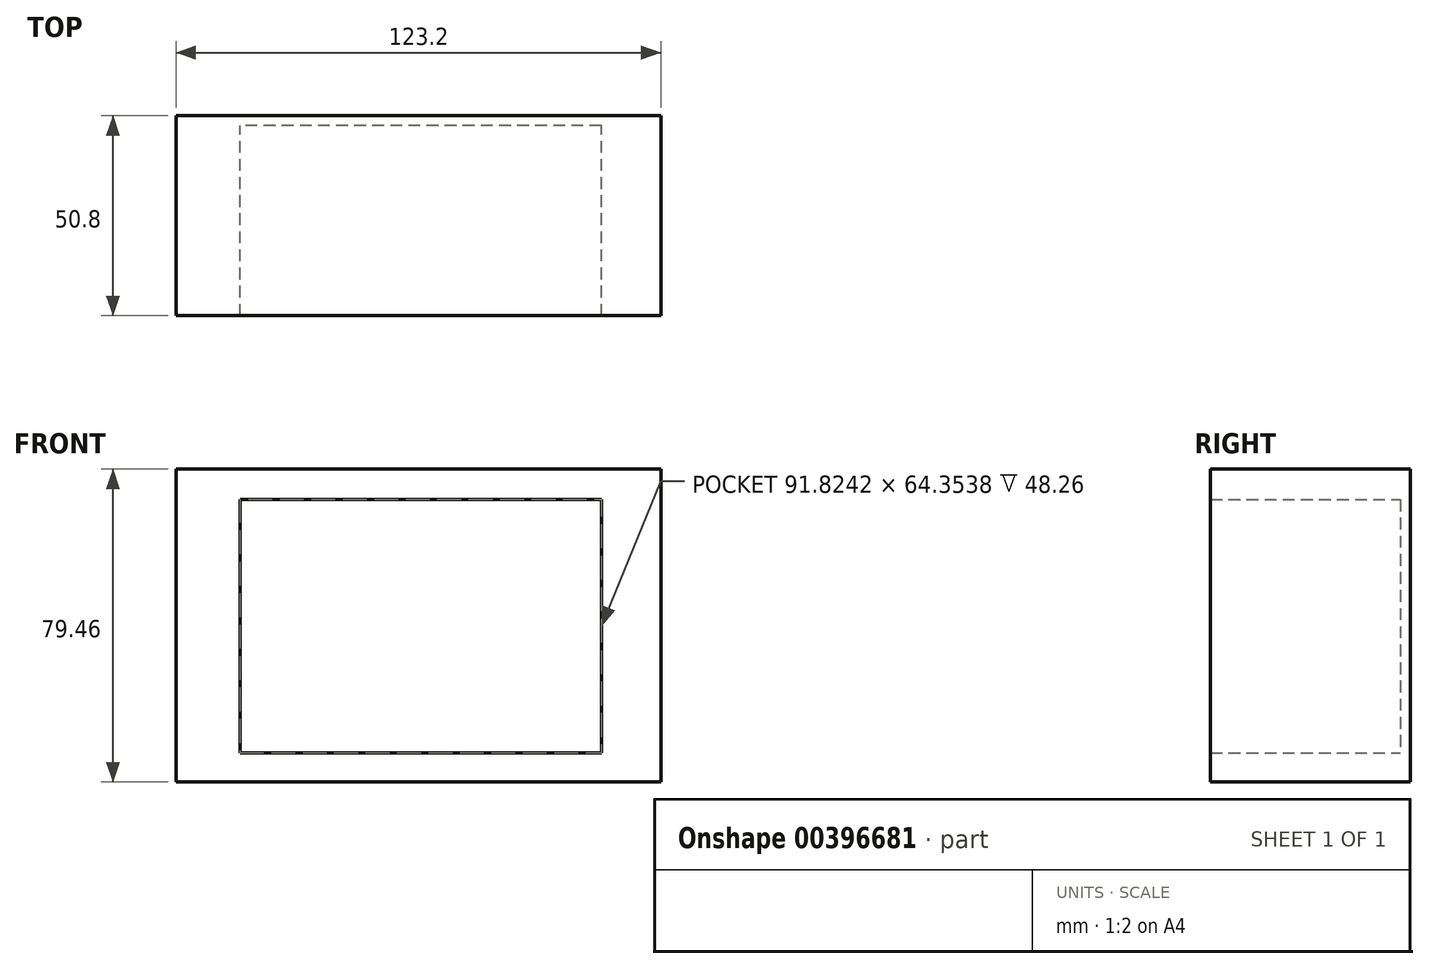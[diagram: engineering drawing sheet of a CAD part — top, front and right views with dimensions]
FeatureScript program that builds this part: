
annotation { "Feature Type Name" : "Feature", "Feature Type Description" : "" }
export const myFeature = defineFeature(function(context is Context, id is Id, definition is map)
    precondition{}
    {
        {
            var Q0;
            Q0=qCreatedBy(makeId("Front.planeOp"),FACE);
            var sketch = newSketch(context, id + "F0", { "sketchPlane" : qUnion([Q0])});
            skLineSegment(sketch, "E0.bottom", {"start": v(-61.6, 39.73) * mm, "end": v(61.6, 39.73) * mm});
            skLineSegment(sketch, "E0.top", {"start": v(-61.6, -39.73) * mm, "end": v(61.6, -39.73) * mm});
            skLineSegment(sketch, "E0.left", {"start": v(-61.6, 39.73) * mm, "end": v(-61.6, -39.73) * mm});
            skLineSegment(sketch, "E0.right", {"start": v(61.6, 39.73) * mm, "end": v(61.6, -39.73) * mm});
            skPoint(sketch, "E0.middle", {"position": v(0, 0) * mm});
            skLineSegment(sketch, "E1", {"start": v(-45.34, 31.98) * mm, "end": v(-45.34, -32.37) * mm});
            skLineSegment(sketch, "E2", {"start": v(-45.34, -32.37) * mm, "end": v(46.49, -32.37) * mm});
            skLineSegment(sketch, "E3", {"start": v(46.49, -32.37) * mm, "end": v(46.49, 31.98) * mm});
            skLineSegment(sketch, "E4", {"start": v(46.49, 31.98) * mm, "end": v(-45.34, 31.98) * mm});
            skSolve(sketch);
        }
        {
            var Q0;
            Q0=makeQuery(id+"F0.imprint","IMPRINT",FACE,{"disambiguationData":[TD([[makeQuery(id+"F0.imprint","IMPRINT",EDGE,{"derivedFrom":sQuery(id+"F0.wireOp",EDGE,"E0.bottom")}),-1.0]])]});
            extrude(context, id + "F1", {"entities" : qUnion([Q0]), "depth" : 50.8 * mm});
        }
        {
            var Q0;
            Q0=makeQuery(id+"F0.imprint","IMPRINT",FACE,{"disambiguationData":[TD([[makeQuery(id+"F0.imprint","IMPRINT",EDGE,{"derivedFrom":sQuery(id+"F0.wireOp",EDGE,"E1")}),1.0]])]});
            extrude(context, id + "F2", {"entities" : qUnion([Q0]), "operationType" : NewBodyOperationType.ADD, "depth" : 2.54 * mm});
        }
    });
